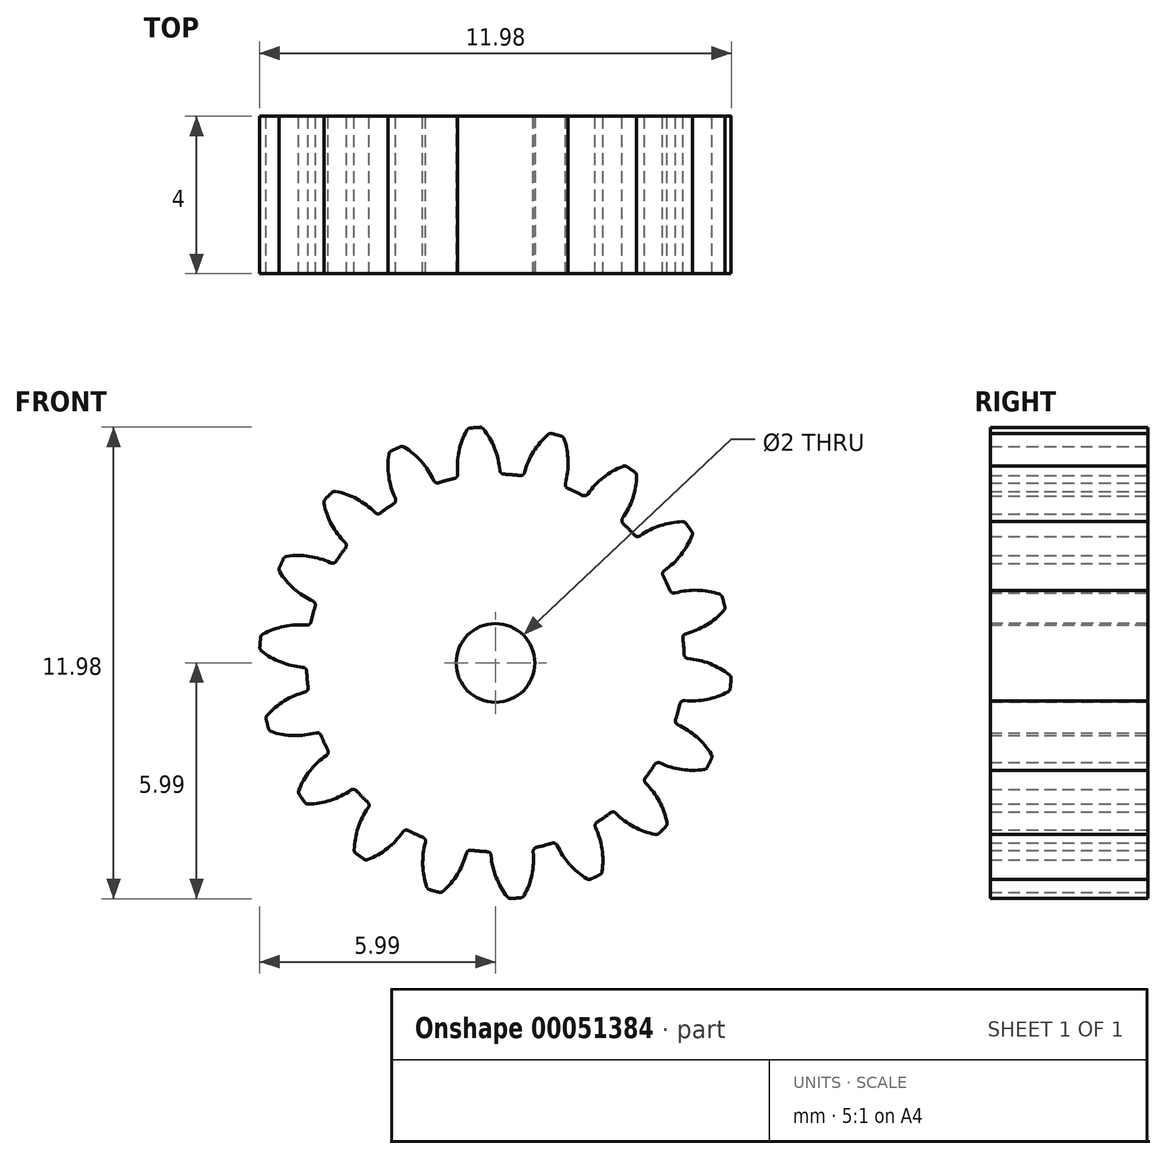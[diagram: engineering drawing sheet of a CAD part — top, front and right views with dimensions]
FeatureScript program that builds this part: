
annotation { "Feature Type Name" : "Feature", "Feature Type Description" : "" }
export const myFeature = defineFeature(function(context is Context, id is Id, definition is map)
    precondition{}
    {
        {
            var Q0;
            Q0=qCreatedBy(makeId("Front.planeOp"),FACE);
            var sketch = newSketch(context, id + "F0", { "sketchPlane" : qUnion([Q0])});
            skCircle(sketch, "E0", {"center": v(0, 0) * mm, "radius": 4.8 * mm, "construction": true});
            skCircle(sketch, "E1", {"center": v(0, 0) * mm, "radius": 5.4 * mm, "construction": true});
            skCircle(sketch, "E2", {"center": v(0, 0) * mm, "radius": 6 * mm, "construction": true});
            skLineSegment(sketch, "E3", {"start": v(0, 0) * mm, "end": v(0, 8.87) * mm, "construction": true});
            skCircle(sketch, "E4.cCircle", {"center": v(0, 0) * mm, "radius": 8.87 * mm, "construction": true});
            skLineSegment(sketch, "E4.0", {"start": v(-0.78, 8.87) * mm, "end": v(0.78, 8.87) * mm, "construction": true});
            skLineSegment(sketch, "E4.1", {"start": v(0.78, 8.87) * mm, "end": v(2.3, 8.6) * mm, "construction": true});
            skLineSegment(sketch, "E4.2", {"start": v(2.3, 8.6) * mm, "end": v(3.76, 8.07) * mm, "construction": true});
            skLineSegment(sketch, "E4.3", {"start": v(3.76, 8.07) * mm, "end": v(5.1, 7.3) * mm, "construction": true});
            skLineSegment(sketch, "E4.4", {"start": v(5.1, 7.3) * mm, "end": v(6.3, 6.3) * mm, "construction": true});
            skLineSegment(sketch, "E4.5", {"start": v(6.3, 6.3) * mm, "end": v(7.3, 5.1) * mm, "construction": true});
            skLineSegment(sketch, "E4.6", {"start": v(7.3, 5.1) * mm, "end": v(8.07, 3.76) * mm, "construction": true});
            skLineSegment(sketch, "E4.7", {"start": v(8.07, 3.76) * mm, "end": v(8.6, 2.3) * mm, "construction": true});
            skLineSegment(sketch, "E4.8", {"start": v(8.6, 2.3) * mm, "end": v(8.87, 0.78) * mm, "construction": true});
            skLineSegment(sketch, "E4.9", {"start": v(8.87, 0.78) * mm, "end": v(8.87, -0.78) * mm, "construction": true});
            skLineSegment(sketch, "E4.10", {"start": v(8.87, -0.78) * mm, "end": v(8.6, -2.3) * mm, "construction": true});
            skLineSegment(sketch, "E4.11", {"start": v(8.6, -2.3) * mm, "end": v(8.07, -3.76) * mm, "construction": true});
            skLineSegment(sketch, "E4.12", {"start": v(8.07, -3.76) * mm, "end": v(7.3, -5.1) * mm, "construction": true});
            skLineSegment(sketch, "E4.13", {"start": v(7.3, -5.1) * mm, "end": v(6.3, -6.3) * mm, "construction": true});
            skLineSegment(sketch, "E4.14", {"start": v(6.3, -6.3) * mm, "end": v(5.1, -7.3) * mm, "construction": true});
            skLineSegment(sketch, "E4.15", {"start": v(5.1, -7.3) * mm, "end": v(3.76, -8.07) * mm, "construction": true});
            skLineSegment(sketch, "E4.16", {"start": v(3.76, -8.07) * mm, "end": v(2.3, -8.6) * mm, "construction": true});
            skLineSegment(sketch, "E4.17", {"start": v(2.3, -8.6) * mm, "end": v(0.78, -8.87) * mm, "construction": true});
            skLineSegment(sketch, "E4.18", {"start": v(0.78, -8.87) * mm, "end": v(-0.78, -8.87) * mm, "construction": true});
            skLineSegment(sketch, "E4.19", {"start": v(-0.78, -8.87) * mm, "end": v(-2.3, -8.6) * mm, "construction": true});
            skLineSegment(sketch, "E4.20", {"start": v(-2.3, -8.6) * mm, "end": v(-3.76, -8.07) * mm, "construction": true});
            skLineSegment(sketch, "E4.21", {"start": v(-3.76, -8.07) * mm, "end": v(-5.1, -7.3) * mm, "construction": true});
            skLineSegment(sketch, "E4.22", {"start": v(-5.1, -7.3) * mm, "end": v(-6.3, -6.3) * mm, "construction": true});
            skLineSegment(sketch, "E4.23", {"start": v(-6.3, -6.3) * mm, "end": v(-7.3, -5.1) * mm, "construction": true});
            skLineSegment(sketch, "E4.24", {"start": v(-7.3, -5.1) * mm, "end": v(-8.07, -3.76) * mm, "construction": true});
            skLineSegment(sketch, "E4.25", {"start": v(-8.07, -3.76) * mm, "end": v(-8.6, -2.3) * mm, "construction": true});
            skLineSegment(sketch, "E4.26", {"start": v(-8.6, -2.3) * mm, "end": v(-8.87, -0.78) * mm, "construction": true});
            skLineSegment(sketch, "E4.27", {"start": v(-8.87, -0.78) * mm, "end": v(-8.87, 0.78) * mm, "construction": true});
            skLineSegment(sketch, "E4.28", {"start": v(-8.87, 0.78) * mm, "end": v(-8.6, 2.3) * mm, "construction": true});
            skLineSegment(sketch, "E4.29", {"start": v(-8.6, 2.3) * mm, "end": v(-8.07, 3.76) * mm, "construction": true});
            skLineSegment(sketch, "E4.30", {"start": v(-8.07, 3.76) * mm, "end": v(-7.3, 5.1) * mm, "construction": true});
            skLineSegment(sketch, "E4.31", {"start": v(-7.3, 5.1) * mm, "end": v(-6.3, 6.3) * mm, "construction": true});
            skLineSegment(sketch, "E4.32", {"start": v(-6.3, 6.3) * mm, "end": v(-5.1, 7.3) * mm, "construction": true});
            skLineSegment(sketch, "E4.33", {"start": v(-5.1, 7.3) * mm, "end": v(-3.76, 8.07) * mm, "construction": true});
            skLineSegment(sketch, "E4.34", {"start": v(-3.76, 8.07) * mm, "end": v(-2.3, 8.6) * mm, "construction": true});
            skLineSegment(sketch, "E4.35", {"start": v(-2.3, 8.6) * mm, "end": v(-0.78, 8.87) * mm, "construction": true});
            skPoint(sketch, "E4.0.midPoint", {"position": v(0, 8.87) * mm});
            skLineSegment(sketch, "E5.0", {"start": v(0, 8.87) * mm, "end": v(1.58, 8.72) * mm, "construction": true});
            skLineSegment(sketch, "E5.1", {"start": v(1.58, 8.72) * mm, "end": v(3.12, 8.3) * mm, "construction": true});
            skLineSegment(sketch, "E5.2", {"start": v(3.12, 8.3) * mm, "end": v(4.55, 7.61) * mm, "construction": true});
            skLineSegment(sketch, "E5.3", {"start": v(4.55, 7.61) * mm, "end": v(5.83, 6.68) * mm, "construction": true});
            skLineSegment(sketch, "E5.4", {"start": v(5.83, 6.68) * mm, "end": v(6.93, 5.53) * mm, "construction": true});
            skLineSegment(sketch, "E5.5", {"start": v(6.93, 5.53) * mm, "end": v(7.8, 4.2) * mm, "construction": true});
            skLineSegment(sketch, "E5.6", {"start": v(7.8, 4.2) * mm, "end": v(8.43, 2.74) * mm, "construction": true});
            skLineSegment(sketch, "E5.7", {"start": v(8.43, 2.74) * mm, "end": v(8.79, 1.2) * mm, "construction": true});
            skLineSegment(sketch, "E5.8", {"start": v(8.79, 1.2) * mm, "end": v(8.86, -0.4) * mm, "construction": true});
            skLineSegment(sketch, "E5.9", {"start": v(8.86, -0.4) * mm, "end": v(8.65, -1.97) * mm, "construction": true});
            skLineSegment(sketch, "E5.10", {"start": v(8.65, -1.97) * mm, "end": v(8.15, -3.49) * mm, "construction": true});
            skLineSegment(sketch, "E5.11", {"start": v(8.15, -3.49) * mm, "end": v(7.4, -4.88) * mm, "construction": true});
            skLineSegment(sketch, "E5.12", {"start": v(7.4, -4.88) * mm, "end": v(6.4, -6.13) * mm, "construction": true});
            skLineSegment(sketch, "E5.13", {"start": v(6.4, -6.13) * mm, "end": v(5.21, -7.17) * mm, "construction": true});
            skLineSegment(sketch, "E5.14", {"start": v(5.21, -7.17) * mm, "end": v(3.85, -7.99) * mm, "construction": true});
            skLineSegment(sketch, "E5.15", {"start": v(3.85, -7.99) * mm, "end": v(2.36, -8.55) * mm, "construction": true});
            skLineSegment(sketch, "E5.16", {"start": v(2.36, -8.55) * mm, "end": v(0.8, -8.83) * mm, "construction": true});
            skLineSegment(sketch, "E5.17", {"start": v(0.8, -8.83) * mm, "end": v(-0.8, -8.83) * mm, "construction": true});
            skLineSegment(sketch, "E5.18", {"start": v(-0.8, -8.83) * mm, "end": v(-2.36, -8.55) * mm, "construction": true});
            skLineSegment(sketch, "E5.19", {"start": v(-2.36, -8.55) * mm, "end": v(-3.85, -7.99) * mm, "construction": true});
            skLineSegment(sketch, "E5.20", {"start": v(-3.85, -7.99) * mm, "end": v(-5.21, -7.17) * mm, "construction": true});
            skLineSegment(sketch, "E5.21", {"start": v(-5.21, -7.17) * mm, "end": v(-6.4, -6.13) * mm, "construction": true});
            skLineSegment(sketch, "E5.22", {"start": v(-6.4, -6.13) * mm, "end": v(-7.4, -4.88) * mm, "construction": true});
            skLineSegment(sketch, "E5.23", {"start": v(-7.4, -4.88) * mm, "end": v(-8.15, -3.49) * mm, "construction": true});
            skLineSegment(sketch, "E5.24", {"start": v(-8.15, -3.49) * mm, "end": v(-8.65, -1.97) * mm, "construction": true});
            skLineSegment(sketch, "E5.25", {"start": v(-8.65, -1.97) * mm, "end": v(-8.86, -0.4) * mm, "construction": true});
            skLineSegment(sketch, "E5.26", {"start": v(-8.86, -0.4) * mm, "end": v(-8.79, 1.2) * mm, "construction": true});
            skLineSegment(sketch, "E5.27", {"start": v(-8.79, 1.2) * mm, "end": v(-8.43, 2.74) * mm, "construction": true});
            skLineSegment(sketch, "E5.28", {"start": v(-8.43, 2.74) * mm, "end": v(-7.8, 4.2) * mm, "construction": true});
            skLineSegment(sketch, "E5.29", {"start": v(-7.8, 4.2) * mm, "end": v(-6.93, 5.53) * mm, "construction": true});
            skLineSegment(sketch, "E5.30", {"start": v(-6.93, 5.53) * mm, "end": v(-5.83, 6.68) * mm, "construction": true});
            skLineSegment(sketch, "E5.31", {"start": v(-5.83, 6.68) * mm, "end": v(-4.55, 7.61) * mm, "construction": true});
            skLineSegment(sketch, "E5.32", {"start": v(-4.55, 7.61) * mm, "end": v(-3.12, 8.3) * mm, "construction": true});
            skLineSegment(sketch, "E5.33", {"start": v(-3.12, 8.3) * mm, "end": v(-1.58, 8.72) * mm, "construction": true});
            skLineSegment(sketch, "E5.34", {"start": v(-1.58, 8.72) * mm, "end": v(0, 8.87) * mm, "construction": true});
            skLineSegment(sketch, "E6", {"start": v(0, 0) * mm, "end": v(-0.78, 8.87) * mm, "construction": true});
            skLineSegment(sketch, "E7", {"start": v(0, 5.4) * mm, "end": v(-9.47, 5.4) * mm, "construction": true});
            skLineSegment(sketch, "E8", {"start": v(0, 5.4) * mm, "end": v(-9.34, 2) * mm, "construction": true});
            skCircle(sketch, "E9", {"center": v(0, 5.4) * mm, "radius": 1.94 * mm, "construction": true});
            skCircle(sketch, "E10", {"center": v(-1.83, 4.74) * mm, "radius": 1.94 * mm, "construction": true});
            skArc(sketch, "E11", {"start": v(-0.3, 5.95) * mm, "mid": v(-0.02, 5.45) * mm, "end": v(0.11, 4.9) * mm});
            skArc(sketch, "E12.MirrorCS", {"start": v(-0.73, 5.9) * mm, "mid": v(-0.93, 5.37) * mm, "end": v(-0.96, 4.8) * mm});
            skArc(sketch, "E13", {"start": v(-0.65, 5.96) * mm, "mid": v(-0.52, 5.98) * mm, "end": v(-0.4, 5.99) * mm});
            skArc(sketch, "E14", {"start": v(-1.04, 4.69) * mm, "mid": v(0.42, -4.78) * mm, "end": v(0.21, 4.8) * mm});
            skPoint(sketch, "E15.visualSharp", {"position": v(-0.95, 4.7) * mm});
            skArc(sketch, "E15.filletArc", {"start": v(-1.04, 4.69) * mm, "mid": v(-0.98, 4.73) * mm, "end": v(-0.96, 4.8) * mm});
            skPoint(sketch, "E16.visualSharp", {"position": v(0.12, 4.8) * mm});
            skArc(sketch, "E16.filletArc", {"start": v(0.11, 4.9) * mm, "mid": v(0.14, 4.83) * mm, "end": v(0.21, 4.8) * mm});
            skPoint(sketch, "E17.visualSharp", {"position": v(-0.7, 5.96) * mm});
            skArc(sketch, "E17.filletArc", {"start": v(-0.65, 5.96) * mm, "mid": v(-0.7, 5.95) * mm, "end": v(-0.73, 5.9) * mm});
            skPoint(sketch, "E18.visualSharp", {"position": v(-0.34, 6) * mm});
            skArc(sketch, "E18.filletArc", {"start": v(-0.3, 5.95) * mm, "mid": v(-0.35, 5.98) * mm, "end": v(-0.4, 5.99) * mm});
            skArc(sketch, "E19.1.0", {"start": v(-2.58, 4.05) * mm, "mid": v(-2.54, 4.1) * mm, "end": v(-2.54, 4.18) * mm});
            skArc(sketch, "E19.1.1", {"start": v(-2.7, 5.3) * mm, "mid": v(-2.7, 4.73) * mm, "end": v(-2.54, 4.18) * mm});
            skArc(sketch, "E19.1.2", {"start": v(-2.65, 5.38) * mm, "mid": v(-2.69, 5.35) * mm, "end": v(-2.7, 5.3) * mm});
            skArc(sketch, "E19.1.3", {"start": v(-2.65, 5.38) * mm, "mid": v(-2.54, 5.44) * mm, "end": v(-2.42, 5.49) * mm});
            skArc(sketch, "E19.1.4", {"start": v(-2.32, 5.48) * mm, "mid": v(-2.37, 5.5) * mm, "end": v(-2.42, 5.49) * mm});
            skArc(sketch, "E19.1.5", {"start": v(-2.32, 5.48) * mm, "mid": v(-1.88, 5.12) * mm, "end": v(-1.57, 4.64) * mm});
            skArc(sketch, "E19.1.6", {"start": v(-1.57, 4.64) * mm, "mid": v(-1.52, 4.58) * mm, "end": v(-1.44, 4.58) * mm});
            skArc(sketch, "E19.2.0", {"start": v(-3.81, 2.92) * mm, "mid": v(-3.79, 3) * mm, "end": v(-3.82, 3.06) * mm});
            skArc(sketch, "E19.2.1", {"start": v(-4.36, 4.06) * mm, "mid": v(-4.16, 3.52) * mm, "end": v(-3.82, 3.06) * mm});
            skArc(sketch, "E19.2.2", {"start": v(-4.33, 4.15) * mm, "mid": v(-4.36, 4.1) * mm, "end": v(-4.36, 4.06) * mm});
            skArc(sketch, "E19.2.3", {"start": v(-4.33, 4.15) * mm, "mid": v(-4.24, 4.24) * mm, "end": v(-4.15, 4.33) * mm});
            skArc(sketch, "E19.2.4", {"start": v(-4.06, 4.36) * mm, "mid": v(-4.1, 4.36) * mm, "end": v(-4.15, 4.33) * mm});
            skArc(sketch, "E19.2.5", {"start": v(-4.06, 4.36) * mm, "mid": v(-3.52, 4.16) * mm, "end": v(-3.06, 3.82) * mm});
            skArc(sketch, "E19.2.6", {"start": v(-3.06, 3.82) * mm, "mid": v(-3, 3.79) * mm, "end": v(-2.92, 3.81) * mm});
            skArc(sketch, "E19.3.0", {"start": v(-4.58, 1.44) * mm, "mid": v(-4.58, 1.52) * mm, "end": v(-4.64, 1.57) * mm});
            skArc(sketch, "E19.3.1", {"start": v(-5.48, 2.32) * mm, "mid": v(-5.12, 1.88) * mm, "end": v(-4.64, 1.57) * mm});
            skArc(sketch, "E19.3.2", {"start": v(-5.49, 2.42) * mm, "mid": v(-5.5, 2.37) * mm, "end": v(-5.48, 2.32) * mm});
            skArc(sketch, "E19.3.3", {"start": v(-5.49, 2.42) * mm, "mid": v(-5.44, 2.54) * mm, "end": v(-5.38, 2.65) * mm});
            skArc(sketch, "E19.3.4", {"start": v(-5.3, 2.7) * mm, "mid": v(-5.35, 2.69) * mm, "end": v(-5.38, 2.65) * mm});
            skArc(sketch, "E19.3.5", {"start": v(-5.3, 2.7) * mm, "mid": v(-4.73, 2.7) * mm, "end": v(-4.18, 2.54) * mm});
            skArc(sketch, "E19.3.6", {"start": v(-4.18, 2.54) * mm, "mid": v(-4.1, 2.54) * mm, "end": v(-4.05, 2.58) * mm});
            skArc(sketch, "E19.4.0", {"start": v(-4.8, -0.21) * mm, "mid": v(-4.83, -0.14) * mm, "end": v(-4.9, -0.11) * mm});
            skArc(sketch, "E19.4.1", {"start": v(-5.95, 0.3) * mm, "mid": v(-5.45, 0.02) * mm, "end": v(-4.9, -0.11) * mm});
            skArc(sketch, "E19.4.2", {"start": v(-5.99, 0.4) * mm, "mid": v(-5.98, 0.35) * mm, "end": v(-5.95, 0.3) * mm});
            skArc(sketch, "E19.4.3", {"start": v(-5.99, 0.4) * mm, "mid": v(-5.98, 0.52) * mm, "end": v(-5.96, 0.65) * mm});
            skArc(sketch, "E19.4.4", {"start": v(-5.9, 0.73) * mm, "mid": v(-5.95, 0.7) * mm, "end": v(-5.96, 0.65) * mm});
            skArc(sketch, "E19.4.5", {"start": v(-5.9, 0.73) * mm, "mid": v(-5.37, 0.93) * mm, "end": v(-4.8, 0.96) * mm});
            skArc(sketch, "E19.4.6", {"start": v(-4.8, 0.96) * mm, "mid": v(-4.73, 0.98) * mm, "end": v(-4.69, 1.04) * mm});
            skArc(sketch, "E19.5.0", {"start": v(-4.43, -1.84) * mm, "mid": v(-4.49, -1.79) * mm, "end": v(-4.56, -1.78) * mm});
            skArc(sketch, "E19.5.1", {"start": v(-5.7, -1.75) * mm, "mid": v(-5.13, -1.85) * mm, "end": v(-4.56, -1.78) * mm});
            skArc(sketch, "E19.5.2", {"start": v(-5.76, -1.67) * mm, "mid": v(-5.74, -1.72) * mm, "end": v(-5.7, -1.75) * mm});
            skArc(sketch, "E19.5.3", {"start": v(-5.76, -1.67) * mm, "mid": v(-5.8, -1.55) * mm, "end": v(-5.83, -1.43) * mm});
            skArc(sketch, "E19.5.4", {"start": v(-5.8, -1.33) * mm, "mid": v(-5.83, -1.38) * mm, "end": v(-5.83, -1.43) * mm});
            skArc(sketch, "E19.5.5", {"start": v(-5.8, -1.33) * mm, "mid": v(-5.37, -0.97) * mm, "end": v(-4.84, -0.74) * mm});
            skArc(sketch, "E19.5.6", {"start": v(-4.84, -0.74) * mm, "mid": v(-4.78, -0.7) * mm, "end": v(-4.76, -0.62) * mm});
            skArc(sketch, "E19.6.0", {"start": v(-3.54, -3.25) * mm, "mid": v(-3.6, -3.21) * mm, "end": v(-3.68, -3.23) * mm});
            skArc(sketch, "E19.6.1", {"start": v(-4.75, -3.59) * mm, "mid": v(-4.19, -3.49) * mm, "end": v(-3.68, -3.23) * mm});
            skArc(sketch, "E19.6.2", {"start": v(-4.84, -3.54) * mm, "mid": v(-4.8, -3.58) * mm, "end": v(-4.75, -3.59) * mm});
            skArc(sketch, "E19.6.3", {"start": v(-4.84, -3.54) * mm, "mid": v(-4.91, -3.44) * mm, "end": v(-4.99, -3.34) * mm});
            skArc(sketch, "E19.6.4", {"start": v(-5, -3.24) * mm, "mid": v(-5, -3.29) * mm, "end": v(-4.99, -3.34) * mm});
            skArc(sketch, "E19.6.5", {"start": v(-5, -3.24) * mm, "mid": v(-4.71, -2.74) * mm, "end": v(-4.3, -2.35) * mm});
            skArc(sketch, "E19.6.6", {"start": v(-4.3, -2.35) * mm, "mid": v(-4.25, -2.29) * mm, "end": v(-4.26, -2.21) * mm});
            skArc(sketch, "E19.7.0", {"start": v(-2.21, -4.26) * mm, "mid": v(-2.29, -4.25) * mm, "end": v(-2.35, -4.3) * mm});
            skArc(sketch, "E19.7.1", {"start": v(-3.24, -5) * mm, "mid": v(-2.74, -4.71) * mm, "end": v(-2.35, -4.3) * mm});
            skArc(sketch, "E19.7.2", {"start": v(-3.34, -4.99) * mm, "mid": v(-3.29, -5) * mm, "end": v(-3.24, -5) * mm});
            skArc(sketch, "E19.7.3", {"start": v(-3.34, -4.99) * mm, "mid": v(-3.44, -4.91) * mm, "end": v(-3.54, -4.84) * mm});
            skArc(sketch, "E19.7.4", {"start": v(-3.59, -4.75) * mm, "mid": v(-3.58, -4.8) * mm, "end": v(-3.54, -4.84) * mm});
            skArc(sketch, "E19.7.5", {"start": v(-3.59, -4.75) * mm, "mid": v(-3.49, -4.19) * mm, "end": v(-3.23, -3.68) * mm});
            skArc(sketch, "E19.7.6", {"start": v(-3.23, -3.68) * mm, "mid": v(-3.21, -3.6) * mm, "end": v(-3.25, -3.54) * mm});
            skArc(sketch, "E19.8.0", {"start": v(-0.62, -4.76) * mm, "mid": v(-0.7, -4.78) * mm, "end": v(-0.74, -4.84) * mm});
            skArc(sketch, "E19.8.1", {"start": v(-1.33, -5.8) * mm, "mid": v(-0.97, -5.37) * mm, "end": v(-0.74, -4.84) * mm});
            skArc(sketch, "E19.8.2", {"start": v(-1.43, -5.83) * mm, "mid": v(-1.38, -5.83) * mm, "end": v(-1.33, -5.8) * mm});
            skArc(sketch, "E19.8.3", {"start": v(-1.43, -5.83) * mm, "mid": v(-1.55, -5.8) * mm, "end": v(-1.67, -5.76) * mm});
            skArc(sketch, "E19.8.4", {"start": v(-1.75, -5.7) * mm, "mid": v(-1.72, -5.74) * mm, "end": v(-1.67, -5.76) * mm});
            skArc(sketch, "E19.8.5", {"start": v(-1.75, -5.7) * mm, "mid": v(-1.85, -5.13) * mm, "end": v(-1.78, -4.56) * mm});
            skArc(sketch, "E19.8.6", {"start": v(-1.78, -4.56) * mm, "mid": v(-1.79, -4.49) * mm, "end": v(-1.84, -4.43) * mm});
            skArc(sketch, "E19.9.0", {"start": v(1.04, -4.69) * mm, "mid": v(0.98, -4.73) * mm, "end": v(0.96, -4.8) * mm});
            skArc(sketch, "E19.9.1", {"start": v(0.73, -5.9) * mm, "mid": v(0.93, -5.37) * mm, "end": v(0.96, -4.8) * mm});
            skArc(sketch, "E19.9.2", {"start": v(0.65, -5.96) * mm, "mid": v(0.7, -5.95) * mm, "end": v(0.73, -5.9) * mm});
            skArc(sketch, "E19.9.3", {"start": v(0.65, -5.96) * mm, "mid": v(0.52, -5.98) * mm, "end": v(0.4, -5.99) * mm});
            skArc(sketch, "E19.9.4", {"start": v(0.3, -5.95) * mm, "mid": v(0.35, -5.98) * mm, "end": v(0.4, -5.99) * mm});
            skArc(sketch, "E19.9.5", {"start": v(0.3, -5.95) * mm, "mid": v(0.02, -5.45) * mm, "end": v(-0.11, -4.9) * mm});
            skArc(sketch, "E19.9.6", {"start": v(-0.11, -4.9) * mm, "mid": v(-0.14, -4.83) * mm, "end": v(-0.21, -4.8) * mm});
            skArc(sketch, "E19.10.0", {"start": v(2.58, -4.05) * mm, "mid": v(2.54, -4.1) * mm, "end": v(2.54, -4.18) * mm});
            skArc(sketch, "E19.10.1", {"start": v(2.7, -5.3) * mm, "mid": v(2.7, -4.73) * mm, "end": v(2.54, -4.18) * mm});
            skArc(sketch, "E19.10.2", {"start": v(2.65, -5.38) * mm, "mid": v(2.69, -5.35) * mm, "end": v(2.7, -5.3) * mm});
            skArc(sketch, "E19.10.3", {"start": v(2.65, -5.38) * mm, "mid": v(2.54, -5.44) * mm, "end": v(2.42, -5.49) * mm});
            skArc(sketch, "E19.10.4", {"start": v(2.32, -5.48) * mm, "mid": v(2.37, -5.5) * mm, "end": v(2.42, -5.49) * mm});
            skArc(sketch, "E19.10.5", {"start": v(2.32, -5.48) * mm, "mid": v(1.88, -5.12) * mm, "end": v(1.57, -4.64) * mm});
            skArc(sketch, "E19.10.6", {"start": v(1.57, -4.64) * mm, "mid": v(1.52, -4.58) * mm, "end": v(1.44, -4.58) * mm});
            skArc(sketch, "E19.11.0", {"start": v(3.81, -2.92) * mm, "mid": v(3.79, -3) * mm, "end": v(3.82, -3.06) * mm});
            skArc(sketch, "E19.11.1", {"start": v(4.36, -4.06) * mm, "mid": v(4.16, -3.52) * mm, "end": v(3.82, -3.06) * mm});
            skArc(sketch, "E19.11.2", {"start": v(4.33, -4.15) * mm, "mid": v(4.36, -4.1) * mm, "end": v(4.36, -4.06) * mm});
            skArc(sketch, "E19.11.3", {"start": v(4.33, -4.15) * mm, "mid": v(4.24, -4.24) * mm, "end": v(4.15, -4.33) * mm});
            skArc(sketch, "E19.11.4", {"start": v(4.06, -4.36) * mm, "mid": v(4.1, -4.36) * mm, "end": v(4.15, -4.33) * mm});
            skArc(sketch, "E19.11.5", {"start": v(4.06, -4.36) * mm, "mid": v(3.52, -4.16) * mm, "end": v(3.06, -3.82) * mm});
            skArc(sketch, "E19.11.6", {"start": v(3.06, -3.82) * mm, "mid": v(3, -3.79) * mm, "end": v(2.92, -3.81) * mm});
            skArc(sketch, "E19.12.0", {"start": v(4.58, -1.44) * mm, "mid": v(4.58, -1.52) * mm, "end": v(4.64, -1.57) * mm});
            skArc(sketch, "E19.12.1", {"start": v(5.48, -2.32) * mm, "mid": v(5.12, -1.88) * mm, "end": v(4.64, -1.57) * mm});
            skArc(sketch, "E19.12.2", {"start": v(5.49, -2.42) * mm, "mid": v(5.5, -2.37) * mm, "end": v(5.48, -2.32) * mm});
            skArc(sketch, "E19.12.3", {"start": v(5.49, -2.42) * mm, "mid": v(5.44, -2.54) * mm, "end": v(5.38, -2.65) * mm});
            skArc(sketch, "E19.12.4", {"start": v(5.3, -2.7) * mm, "mid": v(5.35, -2.69) * mm, "end": v(5.38, -2.65) * mm});
            skArc(sketch, "E19.12.5", {"start": v(5.3, -2.7) * mm, "mid": v(4.73, -2.7) * mm, "end": v(4.18, -2.54) * mm});
            skArc(sketch, "E19.12.6", {"start": v(4.18, -2.54) * mm, "mid": v(4.1, -2.54) * mm, "end": v(4.05, -2.58) * mm});
            skArc(sketch, "E19.13.0", {"start": v(4.8, 0.21) * mm, "mid": v(4.83, 0.14) * mm, "end": v(4.9, 0.11) * mm});
            skArc(sketch, "E19.13.1", {"start": v(5.95, -0.3) * mm, "mid": v(5.45, -0.02) * mm, "end": v(4.9, 0.11) * mm});
            skArc(sketch, "E19.13.2", {"start": v(5.99, -0.4) * mm, "mid": v(5.98, -0.35) * mm, "end": v(5.95, -0.3) * mm});
            skArc(sketch, "E19.13.3", {"start": v(5.99, -0.4) * mm, "mid": v(5.98, -0.52) * mm, "end": v(5.96, -0.65) * mm});
            skArc(sketch, "E19.13.4", {"start": v(5.9, -0.73) * mm, "mid": v(5.95, -0.7) * mm, "end": v(5.96, -0.65) * mm});
            skArc(sketch, "E19.13.5", {"start": v(5.9, -0.73) * mm, "mid": v(5.37, -0.93) * mm, "end": v(4.8, -0.96) * mm});
            skArc(sketch, "E19.13.6", {"start": v(4.8, -0.96) * mm, "mid": v(4.73, -0.98) * mm, "end": v(4.69, -1.04) * mm});
            skArc(sketch, "E19.14.0", {"start": v(4.43, 1.84) * mm, "mid": v(4.49, 1.79) * mm, "end": v(4.56, 1.78) * mm});
            skArc(sketch, "E19.14.1", {"start": v(5.7, 1.75) * mm, "mid": v(5.13, 1.85) * mm, "end": v(4.56, 1.78) * mm});
            skArc(sketch, "E19.14.2", {"start": v(5.76, 1.67) * mm, "mid": v(5.74, 1.72) * mm, "end": v(5.7, 1.75) * mm});
            skArc(sketch, "E19.14.3", {"start": v(5.76, 1.67) * mm, "mid": v(5.8, 1.55) * mm, "end": v(5.83, 1.43) * mm});
            skArc(sketch, "E19.14.4", {"start": v(5.8, 1.33) * mm, "mid": v(5.83, 1.38) * mm, "end": v(5.83, 1.43) * mm});
            skArc(sketch, "E19.14.5", {"start": v(5.8, 1.33) * mm, "mid": v(5.37, 0.97) * mm, "end": v(4.84, 0.74) * mm});
            skArc(sketch, "E19.14.6", {"start": v(4.84, 0.74) * mm, "mid": v(4.78, 0.7) * mm, "end": v(4.76, 0.62) * mm});
            skArc(sketch, "E19.15.0", {"start": v(3.54, 3.25) * mm, "mid": v(3.6, 3.21) * mm, "end": v(3.68, 3.23) * mm});
            skArc(sketch, "E19.15.1", {"start": v(4.75, 3.59) * mm, "mid": v(4.19, 3.49) * mm, "end": v(3.68, 3.23) * mm});
            skArc(sketch, "E19.15.2", {"start": v(4.84, 3.54) * mm, "mid": v(4.8, 3.58) * mm, "end": v(4.75, 3.59) * mm});
            skArc(sketch, "E19.15.3", {"start": v(4.84, 3.54) * mm, "mid": v(4.91, 3.44) * mm, "end": v(4.99, 3.34) * mm});
            skArc(sketch, "E19.15.4", {"start": v(5, 3.24) * mm, "mid": v(5, 3.29) * mm, "end": v(4.99, 3.34) * mm});
            skArc(sketch, "E19.15.5", {"start": v(5, 3.24) * mm, "mid": v(4.71, 2.74) * mm, "end": v(4.3, 2.35) * mm});
            skArc(sketch, "E19.15.6", {"start": v(4.3, 2.35) * mm, "mid": v(4.25, 2.29) * mm, "end": v(4.26, 2.21) * mm});
            skArc(sketch, "E19.16.0", {"start": v(2.21, 4.26) * mm, "mid": v(2.29, 4.25) * mm, "end": v(2.35, 4.3) * mm});
            skArc(sketch, "E19.16.1", {"start": v(3.24, 5) * mm, "mid": v(2.74, 4.71) * mm, "end": v(2.35, 4.3) * mm});
            skArc(sketch, "E19.16.2", {"start": v(3.34, 4.99) * mm, "mid": v(3.29, 5) * mm, "end": v(3.24, 5) * mm});
            skArc(sketch, "E19.16.3", {"start": v(3.34, 4.99) * mm, "mid": v(3.44, 4.91) * mm, "end": v(3.54, 4.84) * mm});
            skArc(sketch, "E19.16.4", {"start": v(3.59, 4.75) * mm, "mid": v(3.58, 4.8) * mm, "end": v(3.54, 4.84) * mm});
            skArc(sketch, "E19.16.5", {"start": v(3.59, 4.75) * mm, "mid": v(3.49, 4.19) * mm, "end": v(3.23, 3.68) * mm});
            skArc(sketch, "E19.16.6", {"start": v(3.23, 3.68) * mm, "mid": v(3.21, 3.6) * mm, "end": v(3.25, 3.54) * mm});
            skArc(sketch, "E19.17.0", {"start": v(0.62, 4.76) * mm, "mid": v(0.7, 4.78) * mm, "end": v(0.74, 4.84) * mm});
            skArc(sketch, "E19.17.1", {"start": v(1.33, 5.8) * mm, "mid": v(0.97, 5.37) * mm, "end": v(0.74, 4.84) * mm});
            skArc(sketch, "E19.17.2", {"start": v(1.43, 5.83) * mm, "mid": v(1.38, 5.83) * mm, "end": v(1.33, 5.8) * mm});
            skArc(sketch, "E19.17.3", {"start": v(1.43, 5.83) * mm, "mid": v(1.55, 5.8) * mm, "end": v(1.67, 5.76) * mm});
            skArc(sketch, "E19.17.4", {"start": v(1.75, 5.7) * mm, "mid": v(1.72, 5.74) * mm, "end": v(1.67, 5.76) * mm});
            skArc(sketch, "E19.17.5", {"start": v(1.75, 5.7) * mm, "mid": v(1.85, 5.13) * mm, "end": v(1.78, 4.56) * mm});
            skArc(sketch, "E19.17.6", {"start": v(1.78, 4.56) * mm, "mid": v(1.79, 4.49) * mm, "end": v(1.84, 4.43) * mm});
            skSolve(sketch);
        }
        {
            var Q0;
            Q0 = qSketchRegion(id + "F0", true);
            extrude(context, id + "F1", {"entities" : qUnion([Q0]), "depth" : 4 * mm});
        }
        {
            var Q0;
            Q0=makeQuery(id+"F1.opExtrude","CAP_FACE",FACE,{"disambiguationData":[OSD([sQuery(id+"F0.wireOp",EDGE,"E11"),sQuery(id+"F0.wireOp",EDGE,"E12.MirrorCS"),sQuery(id+"F0.wireOp",EDGE,"E13"),sQuery(id+"F0.wireOp",EDGE,"E14"),sQuery(id+"F0.wireOp",EDGE,"E15.filletArc"),sQuery(id+"F0.wireOp",EDGE,"E16.filletArc"),sQuery(id+"F0.wireOp",EDGE,"E17.filletArc"),sQuery(id+"F0.wireOp",EDGE,"E18.filletArc"),sQuery(id+"F0.wireOp",EDGE,"E19.1.0"),sQuery(id+"F0.wireOp",EDGE,"E19.1.1"),sQuery(id+"F0.wireOp",EDGE,"E19.1.2"),sQuery(id+"F0.wireOp",EDGE,"E19.1.3"),sQuery(id+"F0.wireOp",EDGE,"E19.1.4"),sQuery(id+"F0.wireOp",EDGE,"E19.1.5"),sQuery(id+"F0.wireOp",EDGE,"E19.1.6"),sQuery(id+"F0.wireOp",EDGE,"E19.2.0"),sQuery(id+"F0.wireOp",EDGE,"E19.2.1"),sQuery(id+"F0.wireOp",EDGE,"E19.2.2"),sQuery(id+"F0.wireOp",EDGE,"E19.2.3"),sQuery(id+"F0.wireOp",EDGE,"E19.2.4"),sQuery(id+"F0.wireOp",EDGE,"E19.2.5"),sQuery(id+"F0.wireOp",EDGE,"E19.2.6"),sQuery(id+"F0.wireOp",EDGE,"E19.3.0"),sQuery(id+"F0.wireOp",EDGE,"E19.3.1"),sQuery(id+"F0.wireOp",EDGE,"E19.3.2"),sQuery(id+"F0.wireOp",EDGE,"E19.3.3"),sQuery(id+"F0.wireOp",EDGE,"E19.3.4"),sQuery(id+"F0.wireOp",EDGE,"E19.3.5"),sQuery(id+"F0.wireOp",EDGE,"E19.3.6"),sQuery(id+"F0.wireOp",EDGE,"E19.4.0"),sQuery(id+"F0.wireOp",EDGE,"E19.4.1"),sQuery(id+"F0.wireOp",EDGE,"E19.4.2"),sQuery(id+"F0.wireOp",EDGE,"E19.4.3"),sQuery(id+"F0.wireOp",EDGE,"E19.4.4"),sQuery(id+"F0.wireOp",EDGE,"E19.4.5"),sQuery(id+"F0.wireOp",EDGE,"E19.4.6"),sQuery(id+"F0.wireOp",EDGE,"E19.5.0"),sQuery(id+"F0.wireOp",EDGE,"E19.5.1"),sQuery(id+"F0.wireOp",EDGE,"E19.5.2"),sQuery(id+"F0.wireOp",EDGE,"E19.5.3"),sQuery(id+"F0.wireOp",EDGE,"E19.5.4"),sQuery(id+"F0.wireOp",EDGE,"E19.5.5"),sQuery(id+"F0.wireOp",EDGE,"E19.5.6"),sQuery(id+"F0.wireOp",EDGE,"E19.6.0"),sQuery(id+"F0.wireOp",EDGE,"E19.6.1"),sQuery(id+"F0.wireOp",EDGE,"E19.6.2"),sQuery(id+"F0.wireOp",EDGE,"E19.6.3"),sQuery(id+"F0.wireOp",EDGE,"E19.6.4"),sQuery(id+"F0.wireOp",EDGE,"E19.6.5"),sQuery(id+"F0.wireOp",EDGE,"E19.6.6"),sQuery(id+"F0.wireOp",EDGE,"E19.7.0"),sQuery(id+"F0.wireOp",EDGE,"E19.7.1"),sQuery(id+"F0.wireOp",EDGE,"E19.7.2"),sQuery(id+"F0.wireOp",EDGE,"E19.7.3"),sQuery(id+"F0.wireOp",EDGE,"E19.7.4"),sQuery(id+"F0.wireOp",EDGE,"E19.7.5"),sQuery(id+"F0.wireOp",EDGE,"E19.7.6"),sQuery(id+"F0.wireOp",EDGE,"E19.8.0"),sQuery(id+"F0.wireOp",EDGE,"E19.8.1"),sQuery(id+"F0.wireOp",EDGE,"E19.8.2"),sQuery(id+"F0.wireOp",EDGE,"E19.8.3"),sQuery(id+"F0.wireOp",EDGE,"E19.8.4"),sQuery(id+"F0.wireOp",EDGE,"E19.8.5"),sQuery(id+"F0.wireOp",EDGE,"E19.8.6"),sQuery(id+"F0.wireOp",EDGE,"E19.9.0"),sQuery(id+"F0.wireOp",EDGE,"E19.9.1"),sQuery(id+"F0.wireOp",EDGE,"E19.9.2"),sQuery(id+"F0.wireOp",EDGE,"E19.9.3"),sQuery(id+"F0.wireOp",EDGE,"E19.9.4"),sQuery(id+"F0.wireOp",EDGE,"E19.9.5"),sQuery(id+"F0.wireOp",EDGE,"E19.9.6"),sQuery(id+"F0.wireOp",EDGE,"E19.10.0"),sQuery(id+"F0.wireOp",EDGE,"E19.10.1"),sQuery(id+"F0.wireOp",EDGE,"E19.10.2"),sQuery(id+"F0.wireOp",EDGE,"E19.10.3"),sQuery(id+"F0.wireOp",EDGE,"E19.10.4"),sQuery(id+"F0.wireOp",EDGE,"E19.10.5"),sQuery(id+"F0.wireOp",EDGE,"E19.10.6"),sQuery(id+"F0.wireOp",EDGE,"E19.11.0"),sQuery(id+"F0.wireOp",EDGE,"E19.11.1"),sQuery(id+"F0.wireOp",EDGE,"E19.11.2"),sQuery(id+"F0.wireOp",EDGE,"E19.11.3"),sQuery(id+"F0.wireOp",EDGE,"E19.11.4"),sQuery(id+"F0.wireOp",EDGE,"E19.11.5"),sQuery(id+"F0.wireOp",EDGE,"E19.11.6"),sQuery(id+"F0.wireOp",EDGE,"E19.12.0"),sQuery(id+"F0.wireOp",EDGE,"E19.12.1"),sQuery(id+"F0.wireOp",EDGE,"E19.12.2"),sQuery(id+"F0.wireOp",EDGE,"E19.12.3"),sQuery(id+"F0.wireOp",EDGE,"E19.12.4"),sQuery(id+"F0.wireOp",EDGE,"E19.12.5"),sQuery(id+"F0.wireOp",EDGE,"E19.12.6"),sQuery(id+"F0.wireOp",EDGE,"E19.13.0"),sQuery(id+"F0.wireOp",EDGE,"E19.13.1"),sQuery(id+"F0.wireOp",EDGE,"E19.13.2"),sQuery(id+"F0.wireOp",EDGE,"E19.13.3"),sQuery(id+"F0.wireOp",EDGE,"E19.13.4"),sQuery(id+"F0.wireOp",EDGE,"E19.13.5"),sQuery(id+"F0.wireOp",EDGE,"E19.13.6"),sQuery(id+"F0.wireOp",EDGE,"E19.14.0"),sQuery(id+"F0.wireOp",EDGE,"E19.14.1"),sQuery(id+"F0.wireOp",EDGE,"E19.14.2"),sQuery(id+"F0.wireOp",EDGE,"E19.14.3"),sQuery(id+"F0.wireOp",EDGE,"E19.14.4"),sQuery(id+"F0.wireOp",EDGE,"E19.14.5"),sQuery(id+"F0.wireOp",EDGE,"E19.14.6"),sQuery(id+"F0.wireOp",EDGE,"E19.15.0"),sQuery(id+"F0.wireOp",EDGE,"E19.15.1"),sQuery(id+"F0.wireOp",EDGE,"E19.15.2"),sQuery(id+"F0.wireOp",EDGE,"E19.15.3"),sQuery(id+"F0.wireOp",EDGE,"E19.15.4"),sQuery(id+"F0.wireOp",EDGE,"E19.15.5"),sQuery(id+"F0.wireOp",EDGE,"E19.15.6"),sQuery(id+"F0.wireOp",EDGE,"E19.16.0"),sQuery(id+"F0.wireOp",EDGE,"E19.16.1"),sQuery(id+"F0.wireOp",EDGE,"E19.16.2"),sQuery(id+"F0.wireOp",EDGE,"E19.16.3"),sQuery(id+"F0.wireOp",EDGE,"E19.16.4"),sQuery(id+"F0.wireOp",EDGE,"E19.16.5"),sQuery(id+"F0.wireOp",EDGE,"E19.16.6"),sQuery(id+"F0.wireOp",EDGE,"E19.17.0"),sQuery(id+"F0.wireOp",EDGE,"E19.17.1"),sQuery(id+"F0.wireOp",EDGE,"E19.17.2"),sQuery(id+"F0.wireOp",EDGE,"E19.17.3"),sQuery(id+"F0.wireOp",EDGE,"E19.17.4"),sQuery(id+"F0.wireOp",EDGE,"E19.17.5"),sQuery(id+"F0.wireOp",EDGE,"E19.17.6")])],"isStart":false});
            var sketch = newSketch(context, id + "F2", { "sketchPlane" : qUnion([Q0])});
            skCircle(sketch, "E20", {"center": v(0, 0) * mm, "radius": 1 * mm});
            skSolve(sketch);
        }
        {
            var Q0;
            Q0 = qSketchRegion(id + "F2", true);
            extrude(context, id + "F3", {"entities" : qUnion([Q0]), "operationType" : NewBodyOperationType.REMOVE, "oppositeDirection" : true, "depth" : 25 * mm});
        }
    });
